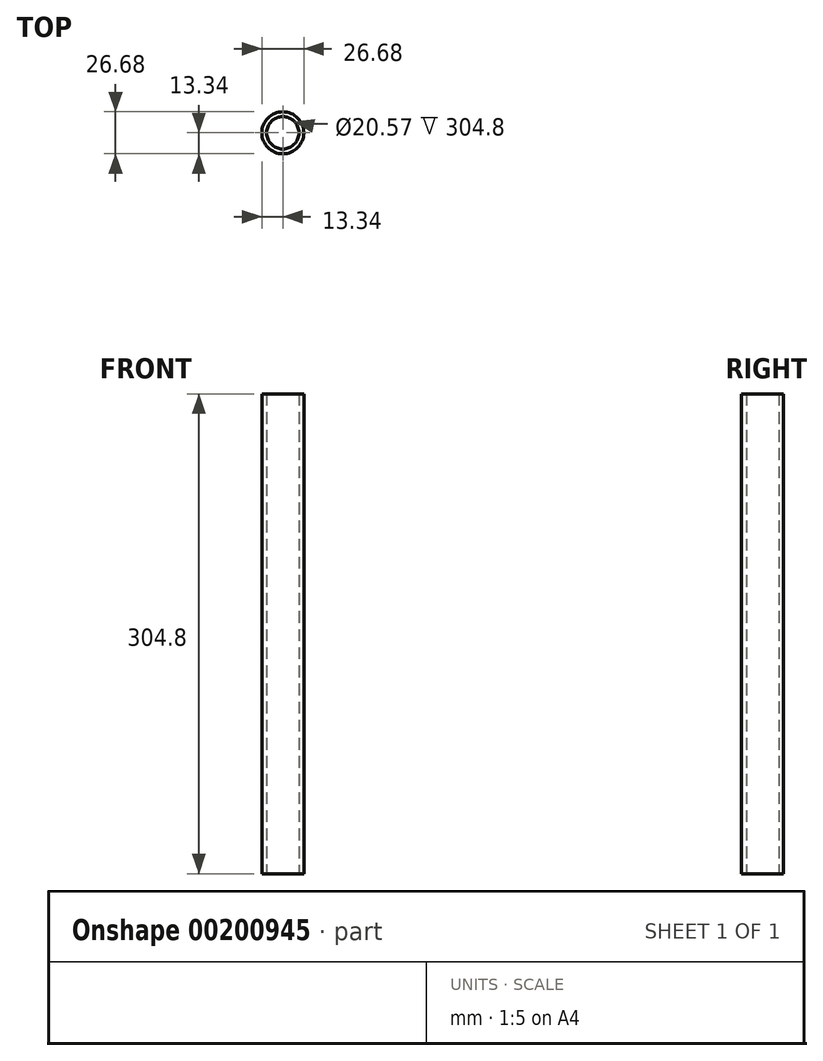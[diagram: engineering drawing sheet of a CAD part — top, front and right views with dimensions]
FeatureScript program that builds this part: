
annotation { "Feature Type Name" : "Feature", "Feature Type Description" : "" }
export const myFeature = defineFeature(function(context is Context, id is Id, definition is map)
    precondition{}
    {
        {
            var Q0;
            Q0=qCreatedBy(makeId("Top.planeOp"),FACE);
            var sketch = newSketch(context, id + "F0", { "sketchPlane" : qUnion([Q0])});
            skCircle(sketch, "E0", {"center": v(0, 0) * mm, "radius": 13.34 * mm});
            skCircle(sketch, "E1", {"center": v(0, 0) * mm, "radius": 10.29 * mm});
            skSolve(sketch);
        }
        {
            var Q0;
            Q0=makeQuery(id+"F0.imprint","IMPRINT",FACE,{"disambiguationData":[TD([[makeQuery(id+"F0.imprint","IMPRINT",EDGE,{"derivedFrom":sQuery(id+"F0.wireOp",EDGE,"E0")}),1.0]])]});
            extrude(context, id + "F1", {"entities" : qUnion([Q0]), "depth" : 304.8 * mm});
        }
    });
